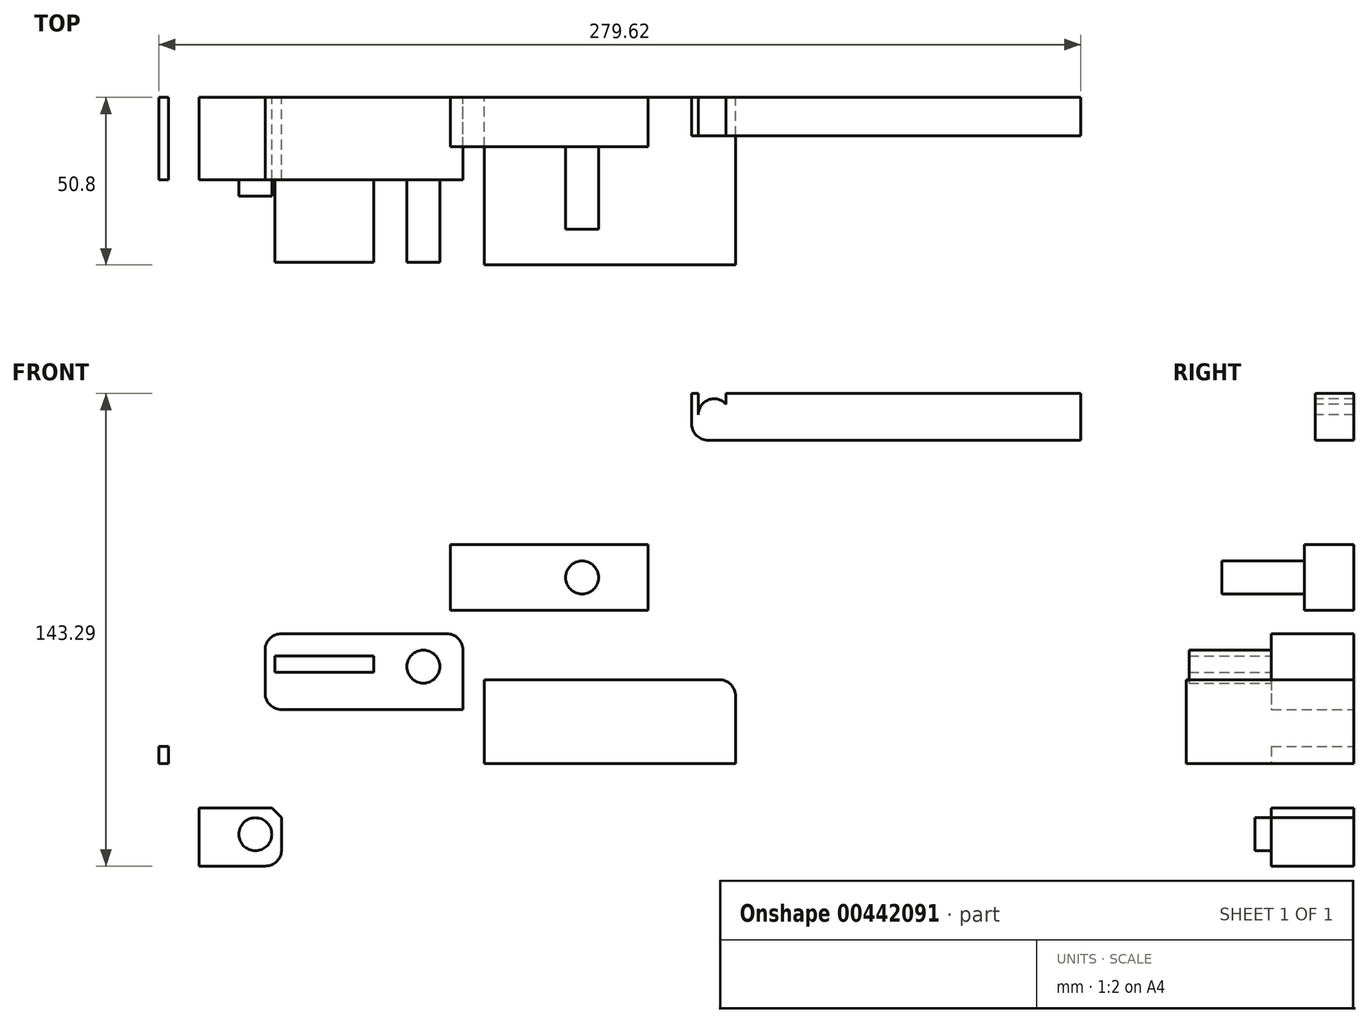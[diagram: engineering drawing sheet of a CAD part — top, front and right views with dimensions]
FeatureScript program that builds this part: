
annotation { "Feature Type Name" : "Feature", "Feature Type Description" : "" }
export const myFeature = defineFeature(function(context is Context, id is Id, definition is map)
    precondition{}
    {
        {
            var Q0;
            Q0=qCreatedBy(makeId("Front.planeOp"),FACE);
            var sketch = newSketch(context, id + "F0", { "sketchPlane" : qUnion([Q0])});
            skLineSegment(sketch, "E0.bottom", {"start": v(-38.1, 25.4) * mm, "end": v(38.1, 25.4) * mm});
            skLineSegment(sketch, "E0.top", {"start": v(-38.1, -25.4) * mm, "end": v(38.1, -25.4) * mm});
            skLineSegment(sketch, "E0.left", {"start": v(-38.1, 25.4) * mm, "end": v(-38.1, -25.4) * mm});
            skLineSegment(sketch, "E0.right", {"start": v(38.1, 25.4) * mm, "end": v(38.1, -25.4) * mm});
            skLineSegment(sketch, "E1", {"start": v(-38.1, 0) * mm, "end": v(38.1, 0) * mm});
            skLineSegment(sketch, "E2", {"start": v(0, 25.4) * mm, "end": v(0, -25.4) * mm});
            skSolve(sketch);
        }
        {
            var Q0;
            Q0=makeQuery(id+"F0.imprint","IMPRINT",FACE,{"disambiguationData":[TD([[makeQuery(id+"F0.imprint","IMPRINT",EDGE,{"derivedFrom":sQuery(id+"F0.wireOp",EDGE,"E0.bottom")}),-1.0]])]});
            extrude(context, id + "F1", {"entities" : qUnion([Q0]), "depth" : 25.4 * mm});
        }
        {
            var Q0;
            Q0=makeQuery(id+"F1.opExtrude","CAP_FACE",FACE,{"disambiguationData":[OSD([sQuery(id+"F0.wireOp",EDGE,"E0.bottom"),sQuery(id+"F0.wireOp",EDGE,"E0.top"),sQuery(id+"F0.wireOp",EDGE,"E0.left"),sQuery(id+"F0.wireOp",EDGE,"E0.right")])],"isStart":false});
            var sketch = newSketch(context, id + "F2", { "sketchPlane" : qUnion([Q0])});
            skCircle(sketch, "E3", {"center": v(0.45, 13.48) * mm, "radius": 8.2 * mm});
            skSolve(sketch);
        }
        {
            var Q0;
            Q0=makeQuery(id+"F1.opExtrude","CAP_FACE",FACE,{"disambiguationData":[OSD([sQuery(id+"F0.wireOp",EDGE,"E0.bottom"),sQuery(id+"F0.wireOp",EDGE,"E0.top"),sQuery(id+"F0.wireOp",EDGE,"E0.left"),sQuery(id+"F0.wireOp",EDGE,"E0.right")])],"isStart":false});
            extrude(context, id + "F3", {"entities" : qUnion([Q0]), "operationType" : NewBodyOperationType.ADD, "depth" : 25.4 * mm});
        }
        {
            var Q0;
            Q0=sQuery(id+"F2.wireOp",EDGE,"E3");
            extrude(context, id + "F4", {"bodyType" : ToolBodyType.SURFACE, "surfaceEntities" : qUnion([Q0]), "depth" : 25.4 * mm});
        }
        {
            var Q0;
            Q0=qCreatedBy(makeId("Front.planeOp"),FACE);
            var sketch = newSketch(context, id + "F5", { "sketchPlane" : qUnion([Q0])});
            skLineSegment(sketch, "E4.bottom", {"start": v(-48.46, 66.38) * mm, "end": v(11.54, 66.38) * mm});
            skLineSegment(sketch, "E4.top", {"start": v(-48.46, 46.38) * mm, "end": v(11.54, 46.38) * mm});
            skLineSegment(sketch, "E4.left", {"start": v(-48.46, 66.38) * mm, "end": v(-48.46, 46.38) * mm});
            skLineSegment(sketch, "E4.right", {"start": v(11.54, 66.38) * mm, "end": v(11.54, 46.38) * mm});
            skSolve(sketch);
        }
        {
            var Q0;
            Q0 = qSketchRegion(id + "F5", true);
            extrude(context, id + "F6", {"entities" : qUnion([Q0]), "depth" : 15 * mm});
        }
        {
            var Q0;
            Q0=makeQuery(id+"F6.opExtrude","CAP_FACE",FACE,{"disambiguationData":[OSD([sQuery(id+"F5.wireOp",EDGE,"E4.bottom"),sQuery(id+"F5.wireOp",EDGE,"E4.top"),sQuery(id+"F5.wireOp",EDGE,"E4.left"),sQuery(id+"F5.wireOp",EDGE,"E4.right")])],"isStart":false});
            var sketch = newSketch(context, id + "F7", { "sketchPlane" : qUnion([Q0])});
            skCircle(sketch, "E5", {"center": v(-8.46, 56.38) * mm, "radius": 5 * mm});
            skSolve(sketch);
        }
        {
            var Q0;
            Q0 = qSketchRegion(id + "F7", true);
            extrude(context, id + "F8", {"entities" : qUnion([Q0]), "operationType" : NewBodyOperationType.ADD, "depth" : 25 * mm});
        }
        {
            var Q0;
            Q0=qCreatedBy(makeId("Front.planeOp"),FACE);
            var sketch = newSketch(context, id + "F9", { "sketchPlane" : qUnion([Q0])});
            skLineSegment(sketch, "E6.bottom", {"start": v(-104.6, 39.35) * mm, "end": v(-44.6, 39.35) * mm});
            skLineSegment(sketch, "E6.top", {"start": v(-104.6, 16.34) * mm, "end": v(-44.6, 16.34) * mm});
            skLineSegment(sketch, "E6.left", {"start": v(-104.6, 39.35) * mm, "end": v(-104.6, 16.34) * mm});
            skLineSegment(sketch, "E6.right", {"start": v(-44.6, 39.35) * mm, "end": v(-44.6, 16.34) * mm});
            skLineSegment(sketch, "E7.bottom", {"start": v(-136.84, 5.17) * mm, "end": v(-133.81, 5.17) * mm});
            skLineSegment(sketch, "E7.top", {"start": v(-136.84, 0) * mm, "end": v(-133.81, 0) * mm});
            skLineSegment(sketch, "E7.left", {"start": v(-136.84, 5.17) * mm, "end": v(-136.84, 0) * mm});
            skLineSegment(sketch, "E7.right", {"start": v(-133.81, 5.17) * mm, "end": v(-133.81, 0) * mm});
            skLineSegment(sketch, "E8.bottom", {"start": v(-124.54, -13.48) * mm, "end": v(-99.54, -13.48) * mm});
            skLineSegment(sketch, "E8.top", {"start": v(-124.54, -31.12) * mm, "end": v(-99.54, -31.12) * mm});
            skLineSegment(sketch, "E8.left", {"start": v(-124.54, -13.48) * mm, "end": v(-124.54, -31.12) * mm});
            skLineSegment(sketch, "E8.right", {"start": v(-99.54, -13.48) * mm, "end": v(-99.54, -31.12) * mm});
            skSolve(sketch);
        }
        {
            var Q0;
            Q0 = qSketchRegion(id + "F9", true);
            extrude(context, id + "F10", {"entities" : qUnion([Q0]), "depth" : 25 * mm, "offsetDistance" : 25 * mm});
        }
        {
            var Q0;
            Q0=makeQuery(id+"F10.opExtrude","SWEPT_EDGE",EDGE,{"disambiguationData":[OSD([sQuery(id+"F9.wireOp",EDGE,"E6.bottom"),sQuery(id+"F9.wireOp",EDGE,"E6.left")])]});
            var Q1;
            Q1=makeQuery(id+"F10.opExtrude","SWEPT_EDGE",EDGE,{"disambiguationData":[OSD([sQuery(id+"F9.wireOp",EDGE,"E6.top"),sQuery(id+"F9.wireOp",EDGE,"E6.left")])]});
            var Q2;
            Q2=makeQuery(id+"F10.opExtrude","SWEPT_EDGE",EDGE,{"disambiguationData":[OSD([sQuery(id+"F9.wireOp",EDGE,"E6.bottom"),sQuery(id+"F9.wireOp",EDGE,"E6.right")])]});
            fillet(context, id + "F11", {"entities" : qUnion([Q0, Q1, Q2]), "radius" : 5 * mm, "tangentPropagation" : true, "allowEdgeOverflow" : false});
        }
        {
            var Q0;
            Q0=makeQuery(id+"F10.opExtrude","CAP_FACE",FACE,{"disambiguationData":[OSD([sQuery(id+"F9.wireOp",EDGE,"E6.bottom"),sQuery(id+"F9.wireOp",EDGE,"E6.top"),sQuery(id+"F9.wireOp",EDGE,"E6.left"),sQuery(id+"F9.wireOp",EDGE,"E6.right")])],"isStart":false});
            var sketch = newSketch(context, id + "F12", { "sketchPlane" : qUnion([Q0])});
            skSolve(sketch);
        }
        {
            var Q0;
            {var subQ0=sQuery(id+"F9.wireOp",EDGE,"E6.bottom");Q0=makeQuery(id+"F12.imprint","IMPRINT",FACE,{"disambiguationData":[TD([[makeQuery(id+"F12.imprint","IMPRINT",EDGE,{"derivedFrom":makeQuery(id+"F10.opExtrude","CAP_EDGE",EDGE,{"disambiguationData":[OSD([subQ0])],"isStart":false})}),-1.0]])]});}
            var sketch = newSketch(context, id + "F13", { "sketchPlane" : qUnion([Q0])});
            skLineSegment(sketch, "E9.bottom", {"start": v(-101.6, 32.62) * mm, "end": v(-71.6, 32.62) * mm});
            skLineSegment(sketch, "E9.top", {"start": v(-101.6, 27.62) * mm, "end": v(-71.6, 27.62) * mm});
            skLineSegment(sketch, "E9.left", {"start": v(-101.6, 32.62) * mm, "end": v(-101.6, 27.62) * mm});
            skLineSegment(sketch, "E9.right", {"start": v(-71.6, 32.62) * mm, "end": v(-71.6, 27.62) * mm});
            skSolve(sketch);
        }
        {
            var Q0;
            Q0=makeQuery(id+"F13.imprint","IMPRINT",FACE,{"disambiguationData":[TD([[makeQuery(id+"F13.imprint","IMPRINT",EDGE,{"derivedFrom":sQuery(id+"F13.wireOp",EDGE,"E9.bottom")}),-1.0]])]});
            extrude(context, id + "F14", {"entities" : qUnion([Q0]), "operationType" : NewBodyOperationType.ADD, "depth" : 25 * mm, "offsetDistance" : 25 * mm});
        }
        {
            var Q0;
            Q0=makeQuery(id+"F10.opExtrude","CAP_FACE",FACE,{"disambiguationData":[OSD([sQuery(id+"F9.wireOp",EDGE,"E8.bottom"),sQuery(id+"F9.wireOp",EDGE,"E8.top"),sQuery(id+"F9.wireOp",EDGE,"E8.left"),sQuery(id+"F9.wireOp",EDGE,"E8.right")])],"isStart":false});
            var sketch = newSketch(context, id + "F15", { "sketchPlane" : qUnion([Q0])});
            skCircle(sketch, "E10", {"center": v(-107.54, -21.48) * mm, "radius": 5 * mm});
            skSolve(sketch);
        }
        {
            var Q0;
            Q0=makeQuery(id+"F15.imprint","IMPRINT",FACE,{"disambiguationData":[TD([[makeQuery(id+"F15.imprint","IMPRINT",EDGE,{"derivedFrom":sQuery(id+"F15.wireOp",EDGE,"E10")}),1.0]])]});
            extrude(context, id + "F16", {"entities" : qUnion([Q0]), "operationType" : NewBodyOperationType.ADD, "depth" : 5 * mm, "offsetDistance" : 25 * mm});
        }
        {
            var Q0;
            Q0=makeQuery(id+"F10.opExtrude","SWEPT_EDGE",EDGE,{"disambiguationData":[OSD([sQuery(id+"F9.wireOp",EDGE,"E8.bottom"),sQuery(id+"F9.wireOp",EDGE,"E8.right")])]});
            chamfer(context, id + "F17", {"entities" : qUnion([Q0]), "width" : 3 * mm, "tangentPropagation" : true});
        }
        {
            var Q0;
            Q0=makeQuery(id+"F10.opExtrude","SWEPT_EDGE",EDGE,{"disambiguationData":[OSD([sQuery(id+"F9.wireOp",EDGE,"E8.top"),sQuery(id+"F9.wireOp",EDGE,"E8.right")])]});
            fillet(context, id + "F18", {"entities" : qUnion([Q0]), "radius" : 5 * mm, "tangentPropagation" : true, "allowEdgeOverflow" : false});
        }
        {
            var Q0;
            {var subQ0=sQuery(id+"F9.wireOp",EDGE,"E6.bottom");Q0=makeQuery(id+"F12.imprint","IMPRINT",FACE,{"disambiguationData":[TD([[makeQuery(id+"F12.imprint","IMPRINT",EDGE,{"derivedFrom":makeQuery(id+"F10.opExtrude","CAP_EDGE",EDGE,{"disambiguationData":[OSD([subQ0])],"isStart":false})}),-1.0]])]});}
            var sketch = newSketch(context, id + "F19", { "sketchPlane" : qUnion([Q0])});
            skCircle(sketch, "E11", {"center": v(-56.6, 29.35) * mm, "radius": 5 * mm});
            skSolve(sketch);
        }
        {
            var Q0;
            Q0 = qSketchRegion(id + "F19", true);
            extrude(context, id + "F20", {"entities" : qUnion([Q0]), "depth" : 25 * mm, "offsetDistance" : 25 * mm});
        }
        {
            var Q0;
            {var subQ0=sQuery(id+"F0.wireOp",EDGE,"E0.right");var subQ1=sQuery(id+"F0.wireOp",EDGE,"E0.bottom");Q0=makeQuery(id+"F3.boolean.opBoolean","MERGE",EDGE,{"derivedFrom":[makeQuery(id+"F1.opExtrude","SWEPT_EDGE",EDGE,{"disambiguationData":[OSD([subQ1,subQ0])]}),makeQuery(id+"F3.opExtrude","SWEPT_EDGE",EDGE,{"disambiguationData":[OSD([subQ1,subQ0])]})]});}
            fillet(context, id + "F21", {"entities" : qUnion([Q0]), "tangentPropagation" : true, "radius" : 5 * mm, "defaultsChanged" : false, "vertexSettings" : [], "allowEdgeOverflow" : false});
        }
        {
            var Q0;
            Q0=qCreatedBy(makeId("Front.planeOp"),FACE);
            var sketch = newSketch(context, id + "F22", { "sketchPlane" : qUnion([Q0])});
            skLineSegment(sketch, "E12.bottom", {"start": v(24.78, 112.17) * mm, "end": v(142.78, 112.17) * mm});
            skLineSegment(sketch, "E12.top", {"start": v(24.78, 97.97) * mm, "end": v(142.78, 97.97) * mm});
            skLineSegment(sketch, "E12.left", {"start": v(24.78, 112.17) * mm, "end": v(24.78, 97.97) * mm});
            skLineSegment(sketch, "E12.right", {"start": v(142.78, 112.17) * mm, "end": v(142.78, 97.97) * mm});
            skSolve(sketch);
        }
        {
            var Q0;
            Q0=makeQuery(id+"F22.imprint","IMPRINT",FACE,{"disambiguationData":[TD([[makeQuery(id+"F22.imprint","IMPRINT",EDGE,{"derivedFrom":sQuery(id+"F22.wireOp",EDGE,"E12.bottom")}),-1.0]])]});
            extrude(context, id + "F23", {"entities" : qUnion([Q0]), "depth" : 11.7 * mm, "offsetDistance" : 25 * mm});
        }
        {
            var Q0;
            Q0=makeQuery(id+"F23.opExtrude","CAP_FACE",FACE,{"disambiguationData":[OSD([sQuery(id+"F22.wireOp",EDGE,"E12.bottom"),sQuery(id+"F22.wireOp",EDGE,"E12.top"),sQuery(id+"F22.wireOp",EDGE,"E12.left"),sQuery(id+"F22.wireOp",EDGE,"E12.right")])],"isStart":false});
            var sketch = newSketch(context, id + "F24", { "sketchPlane" : qUnion([Q0])});
            skCircle(sketch, "E13", {"center": v(31.58, 105.77) * mm, "radius": 4.8 * mm});
            skLineSegment(sketch, "E14", {"start": v(26.78, 105.77) * mm, "end": v(26.78, 112.17) * mm});
            skLineSegment(sketch, "E15", {"start": v(35.18, 112.17) * mm, "end": v(35.18, 108.94) * mm});
            skLineSegment(sketch, "E16", {"start": v(26.78, 112.17) * mm, "end": v(35.18, 112.17) * mm});
            skSolve(sketch);
        }
        {
            var Q0;
            {var subQ0=sQuery(id+"F24.wireOp",EDGE,"E13");var subQ2=makeQuery(id+"F24.imprint","IMPRINT",VERTEX,{"derivedFrom":subQ0});Q0=makeQuery(id+"F24.imprint","IMPRINT",FACE,{"disambiguationData":[TD([[makeQuery(id+"F24.imprint","IMPRINT",EDGE,{"disambiguationData":[TD([[subQ2,-1.0]])],"derivedFrom":subQ0}),1.0]])]});}
            var Q1;
            {var subQ0=sQuery(id+"F24.wireOp",EDGE,"E14");Q1=makeQuery(id+"F24.imprint","IMPRINT",FACE,{"disambiguationData":[TD([[makeQuery(id+"F24.imprint","IMPRINT",EDGE,{"derivedFrom":subQ0}),-1.0]])]});}
            extrude(context, id + "F25", {"entities" : qUnion([Q0, Q1]), "operationType" : NewBodyOperationType.REMOVE, "oppositeDirection" : true, "depth" : 25 * mm, "offsetDistance" : 25 * mm});
        }
        {
            var Q0;
            Q0=makeQuery(id+"F23.opExtrude","SWEPT_EDGE",EDGE,{"disambiguationData":[OSD([sQuery(id+"F22.wireOp",EDGE,"E12.top"),sQuery(id+"F22.wireOp",EDGE,"E12.left")])]});
            fillet(context, id + "F26", {"entities" : qUnion([Q0]), "tangentPropagation" : true, "radius" : 5 * mm, "defaultsChanged" : false, "vertexSettings" : [], "allowEdgeOverflow" : false});
        }
    });
